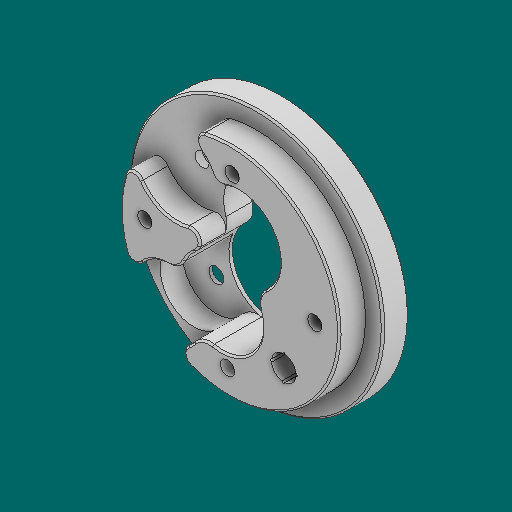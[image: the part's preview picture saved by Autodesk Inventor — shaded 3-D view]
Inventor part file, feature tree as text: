
AUTODESK INVENTOR PART (.ipt)
format: ipt  version: 2023.1 (Build 271208000, 208)  size: 315,904 bytes
history: native  units: in
note: dims shown in document units (in); Inventor stores cm internally (conversion verified against a paired STEP export)
features: sketch x6, other x3
ambient origin geometry x8: Origin, YZ Plane, XZ Plane, XY Plane, X Axis, Y Axis, Z Axis, Center Point
bodies: Solid1 (feature_tree)
feature tree (9):
  other  "UpperRingSeat.ipt"
  other  "Solid1::UpperRingSeat.ipt"
  other  "TaggingFeature1"
  sketch  "Sketch1"  dims[d0=0.3937in]
  sketch  "Sketch2"
  sketch  "Sketch3"
  sketch  "Sketch4"
  sketch  "Sketch5"
  sketch  "Sketch6"
